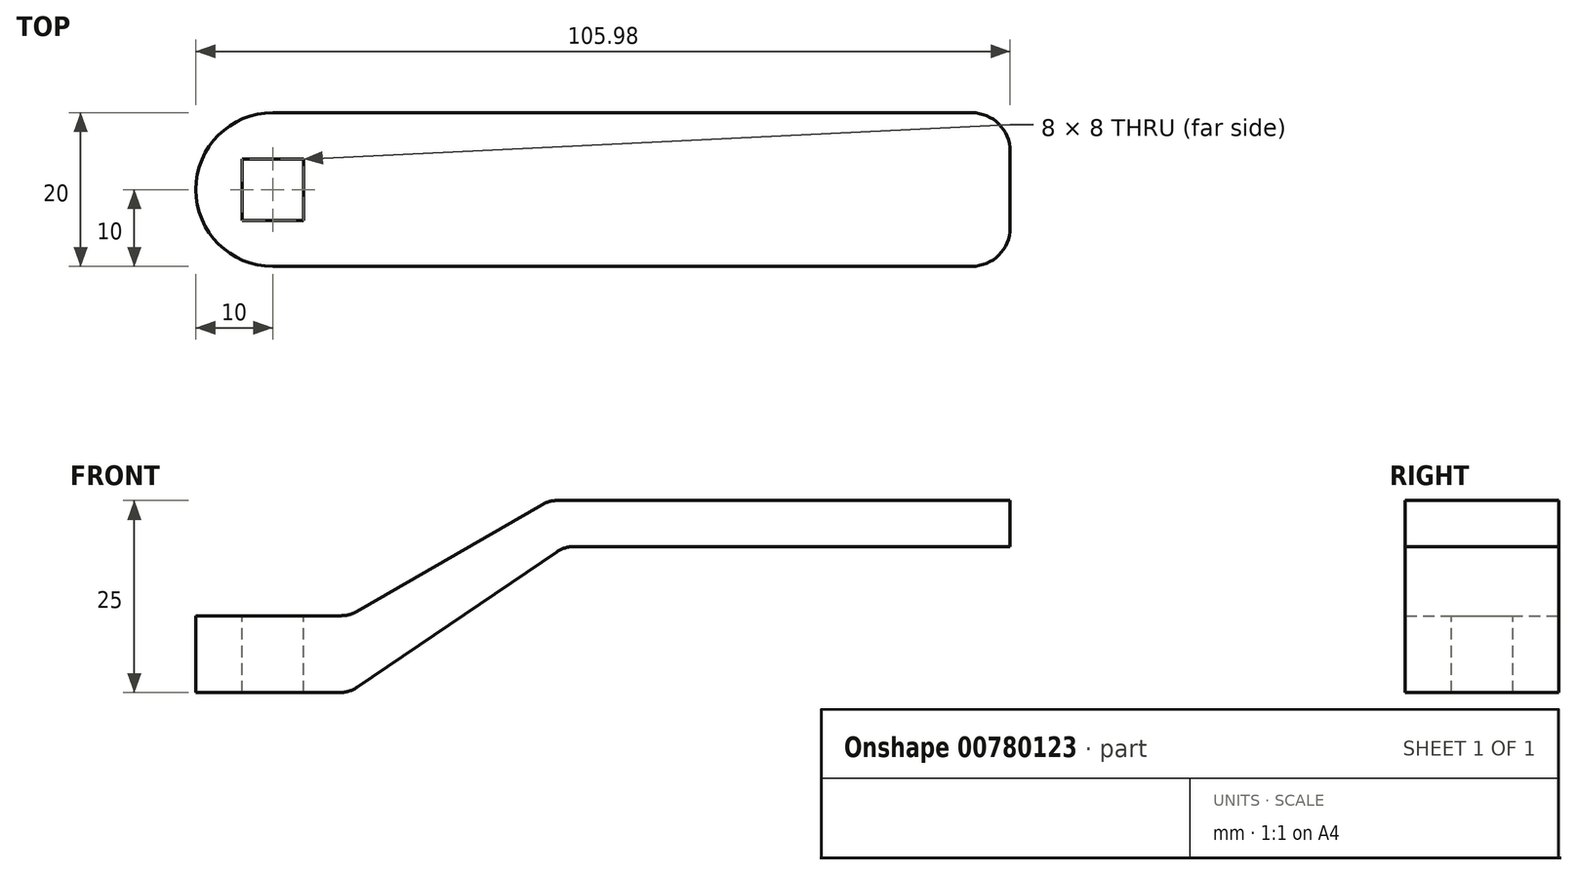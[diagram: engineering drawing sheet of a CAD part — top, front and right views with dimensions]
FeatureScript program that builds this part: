
annotation { "Feature Type Name" : "Feature", "Feature Type Description" : "" }
export const myFeature = defineFeature(function(context is Context, id is Id, definition is map)
    precondition{}
    {
        {
            var Q0;
            Q0=qCreatedBy(makeId("Front.planeOp"),FACE);
            var sketch = newSketch(context, id + "F0", { "sketchPlane" : qUnion([Q0])});
            skLineSegment(sketch, "E0.top", {"start": v(10, 5) * mm, "end": v(-10, 5) * mm});
            skLineSegment(sketch, "E0.right", {"start": v(-10, -5) * mm, "end": v(-10, 5) * mm});
            skPoint(sketch, "E0.middle", {"position": v(0, 0) * mm});
            skLineSegment(sketch, "E1", {"start": v(10, 5) * mm, "end": v(35.98, 20) * mm});
            skLineSegment(sketch, "E2.bottom", {"start": v(35.98, 20) * mm, "end": v(95.98, 20) * mm});
            skLineSegment(sketch, "E2.top", {"start": v(37.98, 14) * mm, "end": v(95.98, 14) * mm});
            skLineSegment(sketch, "E2.right", {"start": v(95.98, 20) * mm, "end": v(95.98, 14) * mm});
            skLineSegment(sketch, "E3", {"start": v(37.98, 14) * mm, "end": v(10, -5) * mm});
            skLineSegment(sketch, "E4", {"start": v(-10, -5) * mm, "end": v(10, -5) * mm});
            skSolve(sketch);
        }
        {
            var Q0;
            Q0=makeQuery(id+"F0.imprint","IMPRINT",FACE,{"disambiguationData":[TD([[makeQuery(id+"F0.imprint","IMPRINT",EDGE,{"derivedFrom":sQuery(id+"F0.wireOp",EDGE,"E0.top")}),1.0]])]});
            extrude(context, id + "F1", {"entities" : qUnion([Q0]), "endBound" : BoundingType.SYMMETRIC, "depth" : 20 * mm, "offsetDistance" : 25 * mm});
        }
        {
            var Q0;
            Q0=makeQuery(id+"F1.opExtrude","SWEPT_FACE",FACE,{"disambiguationData":[OSD([sQuery(id+"F0.wireOp",EDGE,"E0.top")])]});
            var sketch = newSketch(context, id + "F2", { "sketchPlane" : qUnion([Q0])});
            skLineSegment(sketch, "E5.bottom", {"start": v(4, -4) * mm, "end": v(-4, -4) * mm});
            skLineSegment(sketch, "E5.top", {"start": v(4, 4) * mm, "end": v(-4, 4) * mm});
            skLineSegment(sketch, "E5.left", {"start": v(4, -4) * mm, "end": v(4, 4) * mm});
            skLineSegment(sketch, "E5.right", {"start": v(-4, -4) * mm, "end": v(-4, 4) * mm});
            skPoint(sketch, "E5.middle", {"position": v(0, 0) * mm});
            skSolve(sketch);
        }
        {
            var Q0;
            Q0=makeQuery(id+"F2.imprint","IMPRINT",FACE,{"disambiguationData":[TD([[makeQuery(id+"F2.imprint","IMPRINT",EDGE,{"derivedFrom":sQuery(id+"F2.wireOp",EDGE,"E5.bottom")}),-1.0]])]});
            extrude(context, id + "F3", {"entities" : qUnion([Q0]), "operationType" : NewBodyOperationType.REMOVE, "endBound" : BoundingType.UP_TO_NEXT, "oppositeDirection" : true, "depth" : 10 * mm, "offsetDistance" : 25 * mm});
        }
        {
            var Q0;
            Q0=makeQuery(id+"F1.opExtrude","CAP_EDGE",EDGE,{"disambiguationData":[OSD([sQuery(id+"F0.wireOp",EDGE,"E0.right")])],"isStart":false});
            var Q1;
            Q1=makeQuery(id+"F1.opExtrude","CAP_EDGE",EDGE,{"disambiguationData":[OSD([sQuery(id+"F0.wireOp",EDGE,"E0.right")])],"isStart":true});
            fillet(context, id + "F4", {"entities" : qUnion([Q0, Q1]), "radius" : 10 * mm, "tangentPropagation" : true, "allowEdgeOverflow" : false});
        }
        {
            var Q0;
            Q0=makeQuery(id+"F1.opExtrude","SWEPT_EDGE",EDGE,{"disambiguationData":[OSD([sQuery(id+"F0.wireOp",EDGE,"E1"),sQuery(id+"F0.wireOp",EDGE,"E2.bottom")])]});
            var Q1;
            Q1=makeQuery(id+"F1.opExtrude","SWEPT_EDGE",EDGE,{"disambiguationData":[OSD([sQuery(id+"F0.wireOp",EDGE,"E0.top"),sQuery(id+"F0.wireOp",EDGE,"E1")])]});
            var Q2;
            Q2=makeQuery(id+"F1.opExtrude","SWEPT_EDGE",EDGE,{"disambiguationData":[OSD([sQuery(id+"F0.wireOp",EDGE,"E3"),sQuery(id+"F0.wireOp",EDGE,"E4")])]});
            var Q3;
            Q3=makeQuery(id+"F1.opExtrude","SWEPT_EDGE",EDGE,{"disambiguationData":[OSD([sQuery(id+"F0.wireOp",EDGE,"E2.top"),sQuery(id+"F0.wireOp",EDGE,"E3")])]});
            fillet(context, id + "F5", {"entities" : qUnion([Q0, Q1, Q2, Q3]), "radius" : 4 * mm, "tangentPropagation" : true, "allowEdgeOverflow" : false});
        }
        {
            var Q0;
            Q0=makeQuery(id+"F1.opExtrude","CAP_EDGE",EDGE,{"disambiguationData":[OSD([sQuery(id+"F0.wireOp",EDGE,"E2.right")])],"isStart":true});
            var Q1;
            Q1=makeQuery(id+"F1.opExtrude","CAP_EDGE",EDGE,{"disambiguationData":[OSD([sQuery(id+"F0.wireOp",EDGE,"E2.right")])],"isStart":false});
            fillet(context, id + "F6", {"entities" : qUnion([Q0, Q1]), "radius" : 5 * mm, "tangentPropagation" : true, "allowEdgeOverflow" : false});
        }
    });
